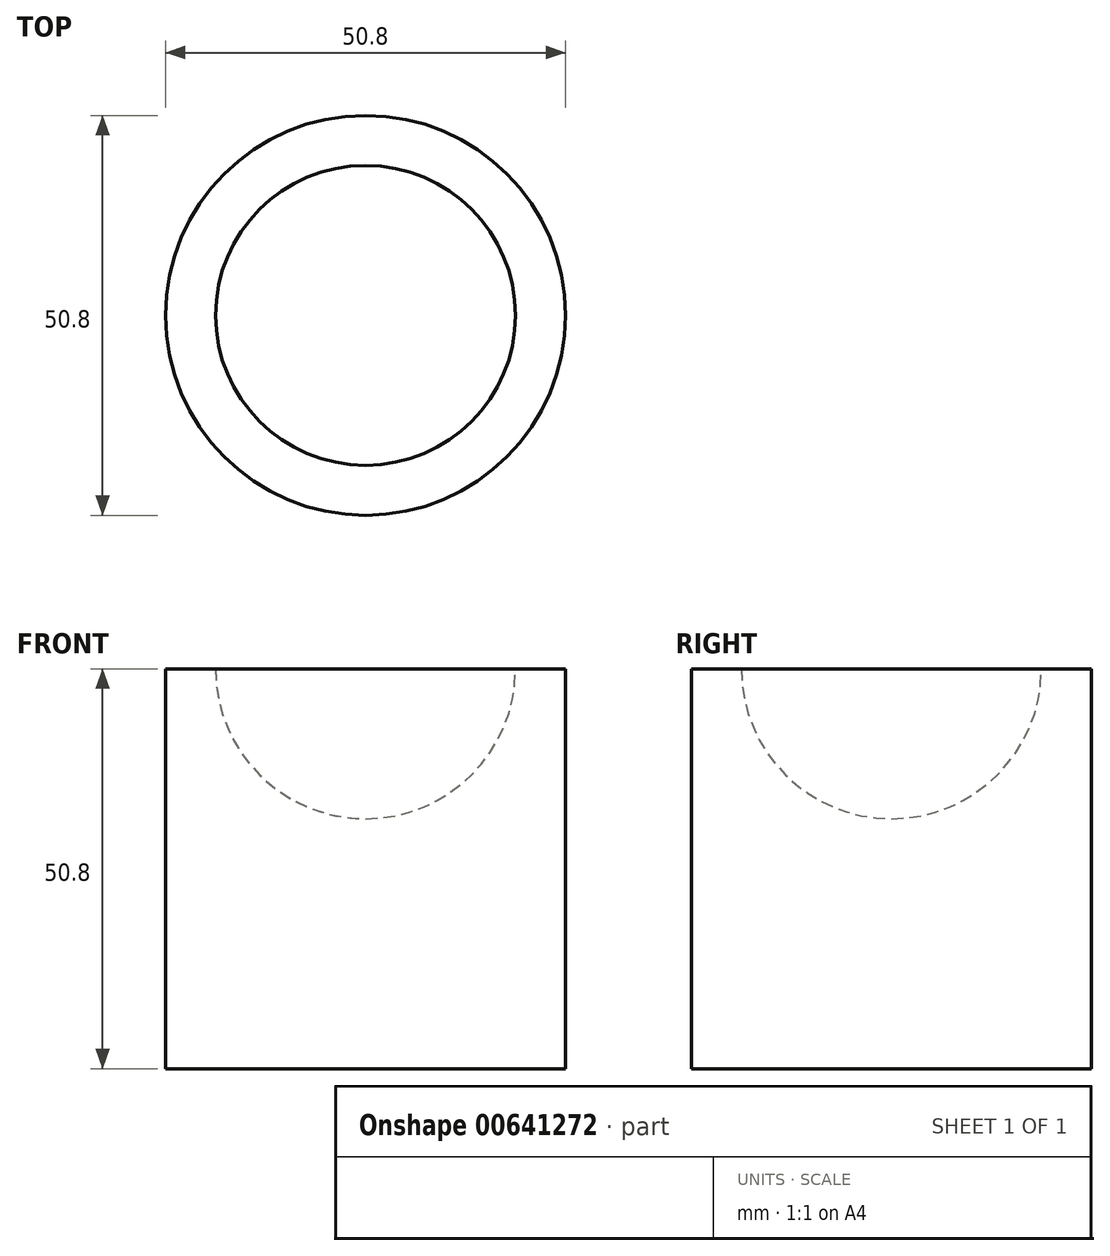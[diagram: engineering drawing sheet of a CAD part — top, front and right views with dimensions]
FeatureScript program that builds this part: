
annotation { "Feature Type Name" : "Feature", "Feature Type Description" : "" }
export const myFeature = defineFeature(function(context is Context, id is Id, definition is map)
    precondition{}
    {
        {
            var Q0;
            Q0=qCreatedBy(makeId("Top.planeOp"),FACE);
            var sketch = newSketch(context, id + "F0", { "sketchPlane" : qUnion([Q0])});
            skCircle(sketch, "E0", {"center": v(0, 0) * mm, "radius": 25.4 * mm});
            skSolve(sketch);
        }
        {
            var Q0;
            Q0 = qSketchRegion(id + "F0", true);
            extrude(context, id + "F1", {"entities" : qUnion([Q0]), "depth" : 50.8 * mm, "offsetDistance" : 25 * mm});
        }
        {
            var Q0;
            Q0=qCreatedBy(makeId("Front.planeOp"),FACE);
            var sketch = newSketch(context, id + "F2", { "sketchPlane" : qUnion([Q0])});
            skLineSegment(sketch, "E1", {"start": v(0, 69.85) * mm, "end": v(0, 31.75) * mm});
            skArc(sketch, "E2", {"start": v(0, 69.85) * mm, "mid": v(-19.05, 50.8) * mm, "end": v(0, 31.75) * mm});
            skSolve(sketch);
        }
        {
            var Q0;
            Q0 = qSketchRegion(id + "F2", true);
            var Q1;
            Q1=sQuery(id+"F2.wireOp",EDGE,"E1");
            revolve(context, id + "F3", {"operationType" : NewBodyOperationType.REMOVE, "entities" : qUnion([Q0]), "axis" : qUnion([Q1]), "revolveType" : RevolveType.ONE_DIRECTION, "oppositeDirection" : true, "angle" : 180 * degree});
        }
        {
            var Q0;
            Q0 = qSketchRegion(id + "F2", true);
            var Q1;
            Q1=makeQuery(id+"F1.opExtrude","SWEPT_FACE",FACE,{"disambiguationData":[OSD([sQuery(id+"F0.wireOp",EDGE,"E0")])]});
            revolve(context, id + "F4", {"operationType" : NewBodyOperationType.REMOVE, "entities" : qUnion([Q0]), "axis" : qUnion([Q1]), "revolveType" : RevolveType.FULL, "oppositeDirection" : true});
        }
    });
